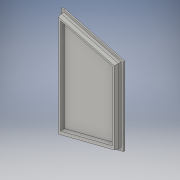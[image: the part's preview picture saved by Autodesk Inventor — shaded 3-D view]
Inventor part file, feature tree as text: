
AUTODESK INVENTOR PART (.ipt)
format: ipt  version: 2016 (Build 200138000, 138)  size: 134,656 bytes
history: native  units: mm
features: extrude x3, sketch x2
ambient origin geometry x8: Origin, YZ Plane, XZ Plane, XY Plane, X Axis, Y Axis, Z Axis, Center Point
bodies: Solid1 (feature_tree)
feature tree (5):
  extrude  "Extrusion1"  Depth=87.0mm
  extrude  "Extrusion2"  Depth=87.0mm
  extrude  "Extrusion3"  Depth=4.0mm TaperAngle=0.0deg
  sketch  "Sketch1"  dims[d0=109.0mm d3=87.0mm]
  sketch  "Sketch3"  dims[d4=152.0mm d5=87.0mm d7=4.0mm d8=0.0mm d9=5.0mm d10=5.0mm d11=5.0mm d12=5.0mm d13=5.0mm d14=-1.745329mm d21=2.0mm d22=0.0mm d24=4.0mm]
